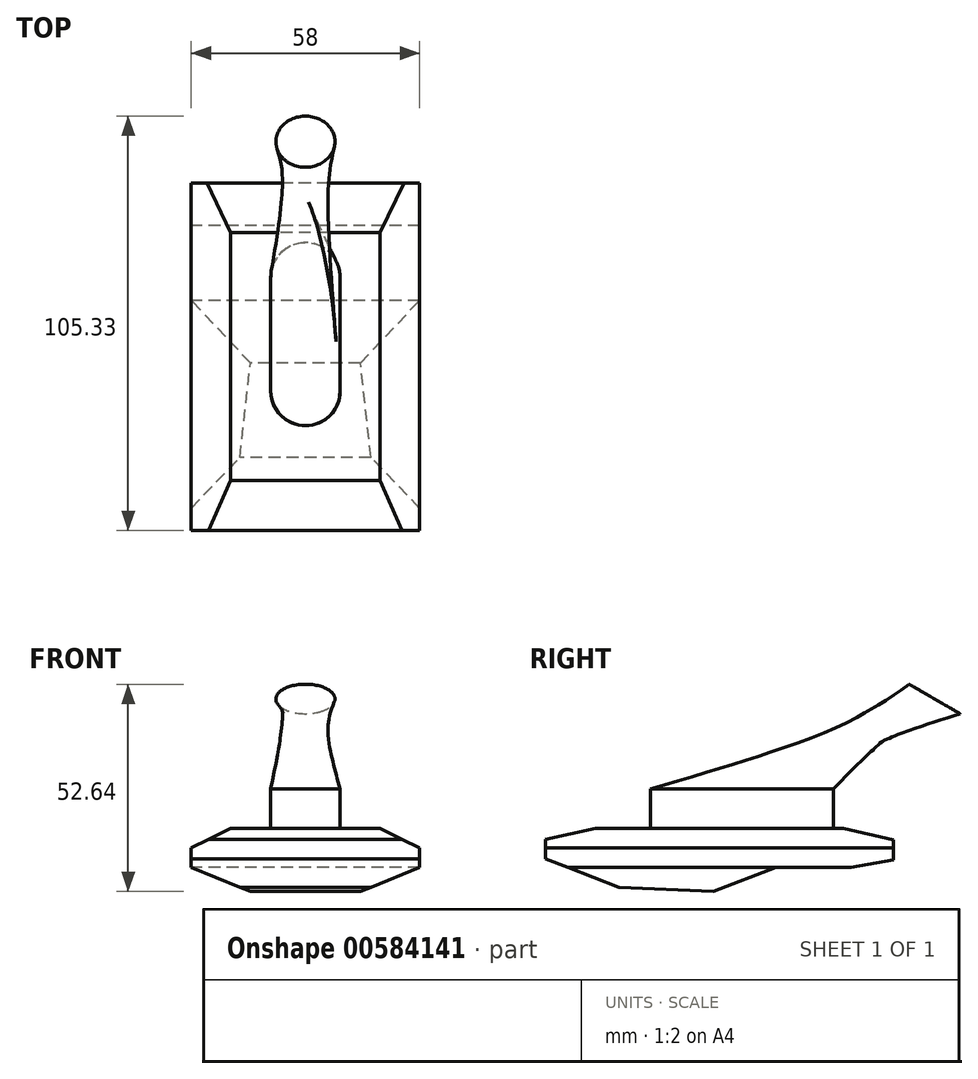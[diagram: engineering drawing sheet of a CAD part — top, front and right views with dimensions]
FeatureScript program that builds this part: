
annotation { "Feature Type Name" : "Feature", "Feature Type Description" : "" }
export const myFeature = defineFeature(function(context is Context, id is Id, definition is map)
    precondition{}
    {
        {
            var Q0;
            Q0=qCreatedBy(makeId("Right.planeOp"),FACE);
            var sketch = newSketch(context, id + "F0", { "sketchPlane" : qUnion([Q0])});
            skLineSegment(sketch, "E0", {"start": v(0, 2.2) * mm, "end": v(0, 7.2) * mm});
            skLineSegment(sketch, "E1", {"start": v(0, 7.2) * mm, "end": v(12.7, 10) * mm});
            skLineSegment(sketch, "E2", {"start": v(12.7, 10) * mm, "end": v(27.7, 10) * mm});
            skLineSegment(sketch, "E3", {"start": v(27.7, 10) * mm, "end": v(75.7, 10) * mm});
            skLineSegment(sketch, "E4", {"start": v(75.7, 10) * mm, "end": v(88.34, 6.98) * mm});
            skLineSegment(sketch, "E5", {"start": v(88.34, 6.98) * mm, "end": v(88.34, 1.98) * mm});
            skLineSegment(sketch, "E6", {"start": v(88.34, 1.98) * mm, "end": v(77.52, 0) * mm});
            skLineSegment(sketch, "E7", {"start": v(77.52, 0) * mm, "end": v(58.52, 0) * mm});
            skLineSegment(sketch, "E8", {"start": v(58.52, 0) * mm, "end": v(42.64, -6.06) * mm});
            skLineSegment(sketch, "E9", {"start": v(42.64, -6.06) * mm, "end": v(18.66, -5) * mm});
            skLineSegment(sketch, "E10", {"start": v(18.66, -5) * mm, "end": v(0, 2.2) * mm});
            skSolve(sketch);
        }
        {
            var Q0;
            Q0 = qSketchRegion(id + "F0", true);
            extrude(context, id + "F1", {"entities" : qUnion([Q0]), "endBound" : BoundingType.SYMMETRIC, "depth" : 58 * mm, "offsetDistance" : 25 * mm});
        }
        {
            var Q0;
            Q0=qCreatedBy(makeId("Front.planeOp"),FACE);
            var sketch = newSketch(context, id + "F2", { "sketchPlane" : qUnion([Q0])});
            skLineSegment(sketch, "E11.0", {"start": v(29, -6.06) * mm, "end": v(-29, -6.06) * mm});
            skLineSegment(sketch, "E12.0", {"start": v(-29, 6.98) * mm, "end": v(-29, 1.98) * mm});
            skLineSegment(sketch, "E12.3", {"start": v(29, 6.98) * mm, "end": v(29, 1.98) * mm});
            skLineSegment(sketch, "E13.0", {"start": v(29, 10) * mm, "end": v(-29, 10) * mm});
            skLineSegment(sketch, "E14", {"start": v(0, 10) * mm, "end": v(-19, 10) * mm});
            skLineSegment(sketch, "E15", {"start": v(-19, 10) * mm, "end": v(-29, 5) * mm});
            skLineSegment(sketch, "E16", {"start": v(-29, 5) * mm, "end": v(-29, 0) * mm});
            skLineSegment(sketch, "E17", {"start": v(-29, 0) * mm, "end": v(-14, -6.06) * mm});
            skLineSegment(sketch, "E18", {"start": v(-14, -6.06) * mm, "end": v(0, -6.06) * mm});
            skLineSegment(sketch, "E19.MirrorCS", {"start": v(0, 10) * mm, "end": v(19, 10) * mm});
            skLineSegment(sketch, "E20.MirrorCS", {"start": v(19, 10) * mm, "end": v(29, 5) * mm});
            skLineSegment(sketch, "E21.MirrorCS", {"start": v(29, 5) * mm, "end": v(29, 0) * mm});
            skLineSegment(sketch, "E22.MirrorCS", {"start": v(29, 0) * mm, "end": v(14, -6.06) * mm});
            skSolve(sketch);
        }
        {
            var Q0;
            Q0 = qSketchRegion(id + "F2", true);
            extrude(context, id + "F3", {"entities" : qUnion([Q0]), "operationType" : NewBodyOperationType.INTERSECT, "endBound" : BoundingType.THROUGH_ALL, "oppositeDirection" : true, "depth" : 25 * mm, "offsetDistance" : 25 * mm});
        }
        {
            var Q0;
            Q0=makeQuery(id+"F1.opExtrude","SWEPT_FACE",FACE,{"disambiguationData":[OSD([sQuery(id+"F0.wireOp",EDGE,"E2"),sQuery(id+"F0.wireOp",EDGE,"E3")])]});
            var sketch = newSketch(context, id + "F4", { "sketchPlane" : qUnion([Q0])});
            skPoint(sketch, "E23.0", {"position": v(0, 12.7) * mm});
            skLineSegment(sketch, "E24.0", {"start": v(19, 12.7) * mm, "end": v(-19, 12.7) * mm});
            skLineSegment(sketch, "E25.0", {"start": v(19, 75.7) * mm, "end": v(19, 12.7) * mm});
            skLineSegment(sketch, "E26.0", {"start": v(-19, 75.7) * mm, "end": v(-19, 12.7) * mm});
            skLineSegment(sketch, "E27.0", {"start": v(19, 75.7) * mm, "end": v(-19, 75.7) * mm});
            skLineSegment(sketch, "E28", {"start": v(0, -8.48) * mm, "end": v(0, 95.98) * mm, "construction": true});
            skLineSegment(sketch, "E29.left", {"start": v(-8.8, 64.4) * mm, "end": v(-8.8, 35.5) * mm});
            skLineSegment(sketch, "E29.right", {"start": v(8.8, 64.4) * mm, "end": v(8.8, 35.5) * mm});
            skPoint(sketch, "E29.middle", {"position": v(0, 49.95) * mm});
            skArc(sketch, "E30", {"start": v(8.8, 35.5) * mm, "mid": v(0, 26.7) * mm, "end": v(-8.8, 35.5) * mm});
            skArc(sketch, "E31", {"start": v(8.8, 64.4) * mm, "mid": v(0, 73.2) * mm, "end": v(-8.8, 64.4) * mm});
            skSolve(sketch);
        }
        {
            var Q0;
            Q0=makeQuery(id+"F4.imprint","IMPRINT",FACE,{"disambiguationData":[TD([[makeQuery(id+"F4.imprint","IMPRINT",EDGE,{"derivedFrom":sQuery(id+"F4.wireOp",EDGE,"E29.left")}),1.0]])]});
            extrude(context, id + "F5", {"entities" : qUnion([Q0]), "operationType" : NewBodyOperationType.ADD, "depth" : 10 * mm, "offsetDistance" : 25 * mm});
        }
        {
            var Q0;
            Q0=makeQuery(id+"F5.opExtrude","CAP_FACE",FACE,{"disambiguationData":[OSD([sQuery(id+"F4.wireOp",EDGE,"E29.left"),sQuery(id+"F4.wireOp",EDGE,"E29.right"),sQuery(id+"F4.wireOp",EDGE,"E30"),sQuery(id+"F4.wireOp",EDGE,"E31")])],"isStart":false});
            var Q1;
            Q1=makeQuery(id+"F1.opExtrude","SWEPT_EDGE",EDGE,{"disambiguationData":[OSD([sQuery(id+"F0.wireOp",EDGE,"E3"),sQuery(id+"F0.wireOp",EDGE,"E4")])]});
            cPlane(context, id + "F6", {"entities" : qUnion([Q0, Q1]), "cplaneType" : CPlaneType.LINE_ANGLE, "offset" : 25 * mm, "angle" : 30 * degree, "width" : 150 * mm, "height" : 150 * mm});
        }
        {
            var Q0;
            Q0=qCreatedBy(id+"F6.planeOp",FACE);
            cPlane(context, id + "F7", {"entities" : qUnion([Q0]), "cplaneType" : CPlaneType.OFFSET, "offset" : 40 * mm, "oppositeDirection" : true, "width" : 150 * mm, "height" : 150 * mm});
        }
        {
            var Q0;
            Q0=qCreatedBy(id+"F7.planeOp",FACE);
            var sketch = newSketch(context, id + "F8", { "sketchPlane" : qUnion([Q0])});
            skCircle(sketch, "E32", {"center": v(0, -64.17) * mm, "radius": 7.5 * mm});
            skSolve(sketch);
        }
        {
            var Q0;
            Q0=makeQuery(id+"F5.opExtrude","CAP_FACE",FACE,{"disambiguationData":[OSD([sQuery(id+"F4.wireOp",EDGE,"E29.left"),sQuery(id+"F4.wireOp",EDGE,"E29.right"),sQuery(id+"F4.wireOp",EDGE,"E30"),sQuery(id+"F4.wireOp",EDGE,"E31")])],"isStart":false});
            var sketch = newSketch(context, id + "F9", { "sketchPlane" : qUnion([Q0])});
            skArc(sketch, "E33.0", {"start": v(8.8, 64.4) * mm, "mid": v(0, 73.2) * mm, "end": v(-8.8, 64.4) * mm});
            skLineSegment(sketch, "E34.0", {"start": v(-8.8, 64.4) * mm, "end": v(-8.8, 35.5) * mm});
            skLineSegment(sketch, "E35.0", {"start": v(8.8, 64.4) * mm, "end": v(8.8, 35.5) * mm});
            skSolve(sketch);
        }
        {
            var Q1;
            Q1=makeQuery(id+"F8.imprint","IMPRINT",FACE,{"disambiguationData":[TD([[makeQuery(id+"F8.imprint","IMPRINT",EDGE,{"derivedFrom":sQuery(id+"F8.wireOp",EDGE,"E32")}),1.0]])]});
            var Q2;
            Q2=makeQuery(id+"F9.imprint","IMPRINT",FACE,{"disambiguationData":[TD([[makeQuery(id+"F9.imprint","IMPRINT",EDGE,{"derivedFrom":sQuery(id+"F9.wireOp",EDGE,"E33.0")}),1.0]])]});
            loft(context, id + "F10", {"operationType" : NewBodyOperationType.ADD, "sheetProfilesArray" : [{ "sheetProfileEntities" : qUnion([Q1]) }, { "sheetProfileEntities" : qUnion([Q2]) }]});
        }
    });
